# Revit family: STH21974BR_27_STH21974PTO_27
name_source: partatom
category: Luminárias
units: mm (PartAtom-declared; Revit-internal decimal feet)

## family parameters
Compartilhado = Não
Corte com vazios quando carregada = Não
Cota do conector redondo = Utilizar diâmetro
Fonte luminosa = Não
Hospedeiro = Forro
Manter orientação da anotação = Não
Número OmniClass = 23.80.70.11
Ponto de cálculo do ambiente = Não
Sempre na vertical = Sim
Tipo de parte = Normal
Título OmniClass = Luminaries for Internal Lighting

## types (2) — shared parameters
Altura = 0.05 m
Comprimento = 2.01 m
Dimerização = Não dimerizável
Fabricante = Stella
Grau de proteção (IP) = IP20
Largura = 0.04 m
Luminoso = Luminoso - 2700K
Modelo = Archi
Temperatura da cor (K) = 2700 K
Tensão Elétrica = 24V
URL = https://stella.com.br
Ângulo de Abertura = 80°
zero-valued in all types: Elevação padrão

## per-type parameters (varying)
| type | Estrutura | Fluxo Luminoso | Fluxo Luminoso STH21974BR/27 | Fluxo Luminoso STH21974PTO/27 | IRC (Índice de reprodução de cores) | Potência | Referência |
| STH21974BR/27 - BRANCO - 2m - 2700K - 1700lm - 80° | Al - Branco | 1700 lm | Sim | Não | >93 (R9 >60) | 46 W | STH21974BR/27 - BRANCO - 2m |
| STH21974PTO/27 - PRETO - 2m - 2700K - 1100lm - 80° | Al - Preto | 1100 lm | Não | Sim | >93 (R9 >60)

>93 (R9 >60)

>93 (R9 >60) | 56 W | STH21974PTO/27 - PRETO - 2m |
